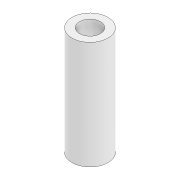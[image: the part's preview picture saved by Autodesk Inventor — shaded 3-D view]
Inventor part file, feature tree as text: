
AUTODESK INVENTOR PART (.ipt)
format: ipt  version: 2020 (Build 240168000, 168)  size: 83,968 bytes
history: native  units: mm
features: extrude x1, sketch x1
ambient origin geometry x8: Origin, YZ Plane, XZ Plane, XY Plane, X Axis, Y Axis, Z Axis, Center Point
bodies: Solid1 (feature_tree)
feature tree (2):
  extrude  "Extrusion1"  Depth=10.0mm
  sketch  "Sketch1"  dims[d0=5.8mm d1=10.0mm d2=30.0mm d3=0.0mm]
